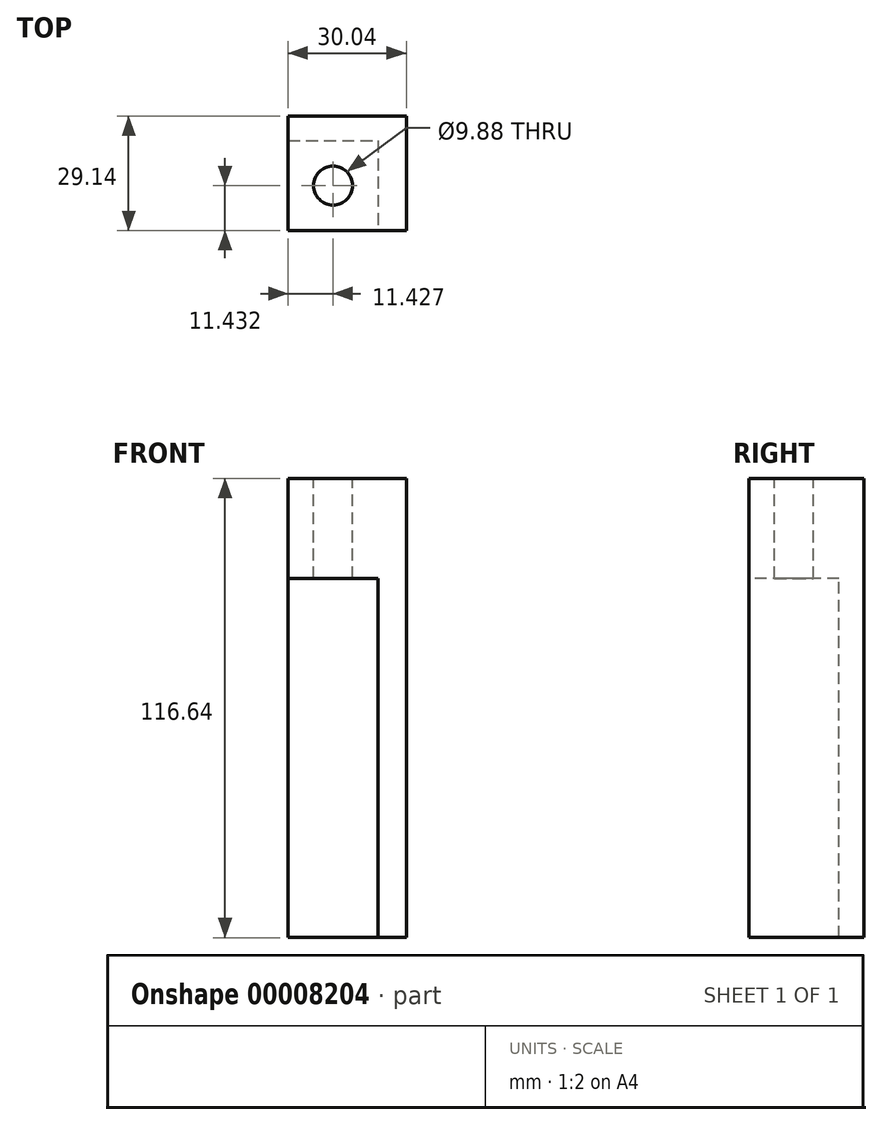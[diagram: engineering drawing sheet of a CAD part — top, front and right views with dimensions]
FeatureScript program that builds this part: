
annotation { "Feature Type Name" : "Feature", "Feature Type Description" : "" }
export const myFeature = defineFeature(function(context is Context, id is Id, definition is map)
    precondition{}
    {
        {
            var Q0;
            Q0=qCreatedBy(makeId("Top.planeOp"),FACE);
            var sketch = newSketch(context, id + "F0", { "sketchPlane" : qUnion([Q0])});
            skLineSegment(sketch, "E0.rect.bottom", {"start": v(-15.02, -14.57) * mm, "end": v(15.02, -14.57) * mm});
            skLineSegment(sketch, "E0.rect.top", {"start": v(-15.02, 14.57) * mm, "end": v(15.02, 14.57) * mm});
            skLineSegment(sketch, "E0.rect.left", {"start": v(-15.02, -14.57) * mm, "end": v(-15.02, 14.57) * mm});
            skLineSegment(sketch, "E0.rect.right", {"start": v(15.02, -14.57) * mm, "end": v(15.02, 14.57) * mm});
            skPoint(sketch, "E0.rect.middle", {"position": v(0, 0) * mm});
            skSolve(sketch);
        }
        {
            var Q0;
            Q0=qSketchRegion(id+"F0",true);
            extrude(context, id + "F1", {"entities" : qUnion([Q0]), "oppositeDirection" : true, "depth" : 200.66 * mm});
        }
        {
            var Q0;
            Q0=makeQuery(id+"F1.opExtrude","SWEPT_FACE",FACE,{"disambiguationData":[OSD([sQuery(id+"F0.wireOp",EDGE,"E0.rect.left")])]});
            var sketch = newSketch(context, id + "F2", { "sketchPlane" : qUnion([Q0])});
            skArc(sketch, "E1", {"start": v(-1.06, -132.08) * mm, "mid": v(-3.6, -129.54) * mm, "end": v(-6.14, -132.08) * mm});
            skArc(sketch, "E2", {"start": v(-6.14, -182.88) * mm, "mid": v(-3.6, -185.42) * mm, "end": v(-1.06, -182.88) * mm});
            skLineSegment(sketch, "E3.left", {"start": v(-6.14, -132.08) * mm, "end": v(-6.14, -182.88) * mm});
            skLineSegment(sketch, "E3.right", {"start": v(-1.06, -132.08) * mm, "end": v(-1.06, -182.88) * mm});
            skSolve(sketch);
        }
        {
            var Q0;
            Q0=qSketchRegion(id+"F2",true);
            extrude(context, id + "F3", {"entities" : qUnion([Q0]), "operationType" : NewBodyOperationType.REMOVE, "endBound" : BoundingType.UP_TO_NEXT, "oppositeDirection" : true, "depth" : 25.4 * mm});
        }
        {
            var Q0;
            Q0=makeQuery(id+"F1.opExtrude","SWEPT_FACE",FACE,{"disambiguationData":[OSD([sQuery(id+"F0.wireOp",EDGE,"E0.rect.left")])]});
            var sketch = newSketch(context, id + "F4", { "sketchPlane" : qUnion([Q0])});
            skArc(sketch, "E4", {"start": v(0.85, -132.08) * mm, "mid": v(-3.6, -127.64) * mm, "end": v(-8.04, -132.08) * mm});
            skArc(sketch, "E5", {"start": v(-8.04, -182.88) * mm, "mid": v(-3.6, -187.33) * mm, "end": v(0.85, -182.88) * mm});
            skLineSegment(sketch, "E6.left", {"start": v(-8.04, -132.08) * mm, "end": v(-8.04, -182.88) * mm});
            skLineSegment(sketch, "E6.right", {"start": v(0.85, -132.08) * mm, "end": v(0.85, -182.88) * mm});
            skSolve(sketch);
        }
        {
            var Q0;
            Q0=qSketchRegion(id+"F4",true);
            extrude(context, id + "F5", {"entities" : qUnion([Q0]), "operationType" : NewBodyOperationType.REMOVE, "oppositeDirection" : true, "depth" : 2.54 * mm});
        }
        {
            var Q0;
            Q0=qCreatedBy(makeId("Top.planeOp"),FACE);
            cPlane(context, id + "F6", {"entities" : qUnion([Q0]), "cplaneType" : CPlaneType.OFFSET, "offset" : 25.4 * mm, "oppositeDirection" : true, "width" : 152.4 * mm, "height" : 152.4 * mm});
        }
        {
            var Q0;
            Q0=qCreatedBy(id+"F6.planeOp",FACE);
            var sketch = newSketch(context, id + "F7", { "sketchPlane" : qUnion([Q0])});
            skCircle(sketch, "E7", {"center": v(-3.6, -3.14) * mm, "radius": 11.43 * mm, "construction": true});
            skCircle(sketch, "E8", {"center": v(-3.6, -3.14) * mm, "radius": 4.95 * mm, "construction": true});
            skLineSegment(sketch, "E9", {"start": v(7.84, 8.3) * mm, "end": v(7.84, -14.57) * mm});
            skLineSegment(sketch, "E10", {"start": v(-15.02, 8.3) * mm, "end": v(7.84, 8.3) * mm});
            skLineSegment(sketch, "E11", {"start": v(-15.02, 8.3) * mm, "end": v(-15.02, -14.57) * mm});
            skLineSegment(sketch, "E12", {"start": v(-15.02, -14.57) * mm, "end": v(7.84, -14.57) * mm});
            skSolve(sketch);
        }
        {
            var Q0;
            Q0=qSketchRegion(id+"F7",true);
            extrude(context, id + "F8", {"entities" : qUnion([Q0]), "operationType" : NewBodyOperationType.REMOVE, "oppositeDirection" : true, "depth" : 46.8 * mm});
        }
        {
            var Q0;
            Q0=makeQuery(id+"F1.opExtrude","CAP_FACE",FACE,{"disambiguationData":[OSD([sQuery(id+"F0.wireOp",EDGE,"E0.rect.bottom"),sQuery(id+"F0.wireOp",EDGE,"E0.rect.top"),sQuery(id+"F0.wireOp",EDGE,"E0.rect.left"),sQuery(id+"F0.wireOp",EDGE,"E0.rect.right")])],"isStart":true});
            var sketch = newSketch(context, id + "F9", { "sketchPlane" : qUnion([Q0])});
            skCircle(sketch, "E13", {"center": v(-3.6, -3.14) * mm, "radius": 4.94 * mm});
            skSolve(sketch);
        }
        {
            var Q0;
            Q0=qSketchRegion(id+"F9",true);
            extrude(context, id + "F10", {"entities" : qUnion([Q0]), "operationType" : NewBodyOperationType.REMOVE, "oppositeDirection" : true, "depth" : 78.54 * mm});
        }
        {
            var Q0;
            Q0=makeQuery(id+"F1.opExtrude","SWEPT_FACE",FACE,{"disambiguationData":[OSD([sQuery(id+"F0.wireOp",EDGE,"E0.rect.left")])]});
            var sketch = newSketch(context, id + "F11", { "sketchPlane" : qUnion([Q0])});
            skLineSegment(sketch, "E14.bottom", {"start": v(-8.3, -72.19) * mm, "end": v(14.57, -72.19) * mm});
            skLineSegment(sketch, "E14.top", {"start": v(-8.3, -116.64) * mm, "end": v(14.57, -116.64) * mm});
            skLineSegment(sketch, "E14.left", {"start": v(-8.3, -72.19) * mm, "end": v(-8.3, -116.64) * mm});
            skLineSegment(sketch, "E14.right", {"start": v(14.57, -72.19) * mm, "end": v(14.57, -116.64) * mm});
            skSolve(sketch);
        }
        {
            var Q0;
            Q0=qSketchRegion(id+"F11",true);
            var Q1;
            Q1=makeQuery(id+"F8.boolean.opBoolean","COPY",FACE,{"derivedFrom":makeQuery(id+"F8.opExtrude","SWEPT_FACE",FACE,{"disambiguationData":[OSD([sQuery(id+"F7.wireOp",EDGE,"E9")])]})});
            extrude(context, id + "F12", {"entities" : qUnion([Q0]), "operationType" : NewBodyOperationType.REMOVE, "endBound" : BoundingType.UP_TO_SURFACE, "oppositeDirection" : true, "endBoundEntityFace" : qUnion([Q1]), "depth" : 25.4 * mm});
        }
        {
            var Q0;
            Q0=makeQuery(id+"F1.opExtrude","SWEPT_FACE",FACE,{"disambiguationData":[OSD([sQuery(id+"F0.wireOp",EDGE,"E0.rect.left")])]});
            var sketch = newSketch(context, id + "F13", { "sketchPlane" : qUnion([Q0])});
            skLineSegment(sketch, "E15.bottom", {"start": v(14.57, -116.64) * mm, "end": v(-14.57, -116.64) * mm});
            skLineSegment(sketch, "E15.top", {"start": v(14.57, -200.66) * mm, "end": v(-14.57, -200.66) * mm});
            skLineSegment(sketch, "E15.left", {"start": v(14.57, -116.64) * mm, "end": v(14.57, -200.66) * mm});
            skLineSegment(sketch, "E15.right", {"start": v(-14.57, -116.64) * mm, "end": v(-14.57, -200.66) * mm});
            skSolve(sketch);
        }
        {
            var Q0;
            Q0=qSketchRegion(id+"F13",true);
            var Q1;
            Q1=makeQuery(id+"F1.opExtrude","SWEPT_FACE",FACE,{"disambiguationData":[OSD([sQuery(id+"F0.wireOp",EDGE,"E0.rect.right")])]});
            extrude(context, id + "F14", {"entities" : qUnion([Q0]), "operationType" : NewBodyOperationType.REMOVE, "endBound" : BoundingType.UP_TO_SURFACE, "oppositeDirection" : true, "endBoundEntityFace" : qUnion([Q1]), "depth" : 25.4 * mm});
        }
    });
